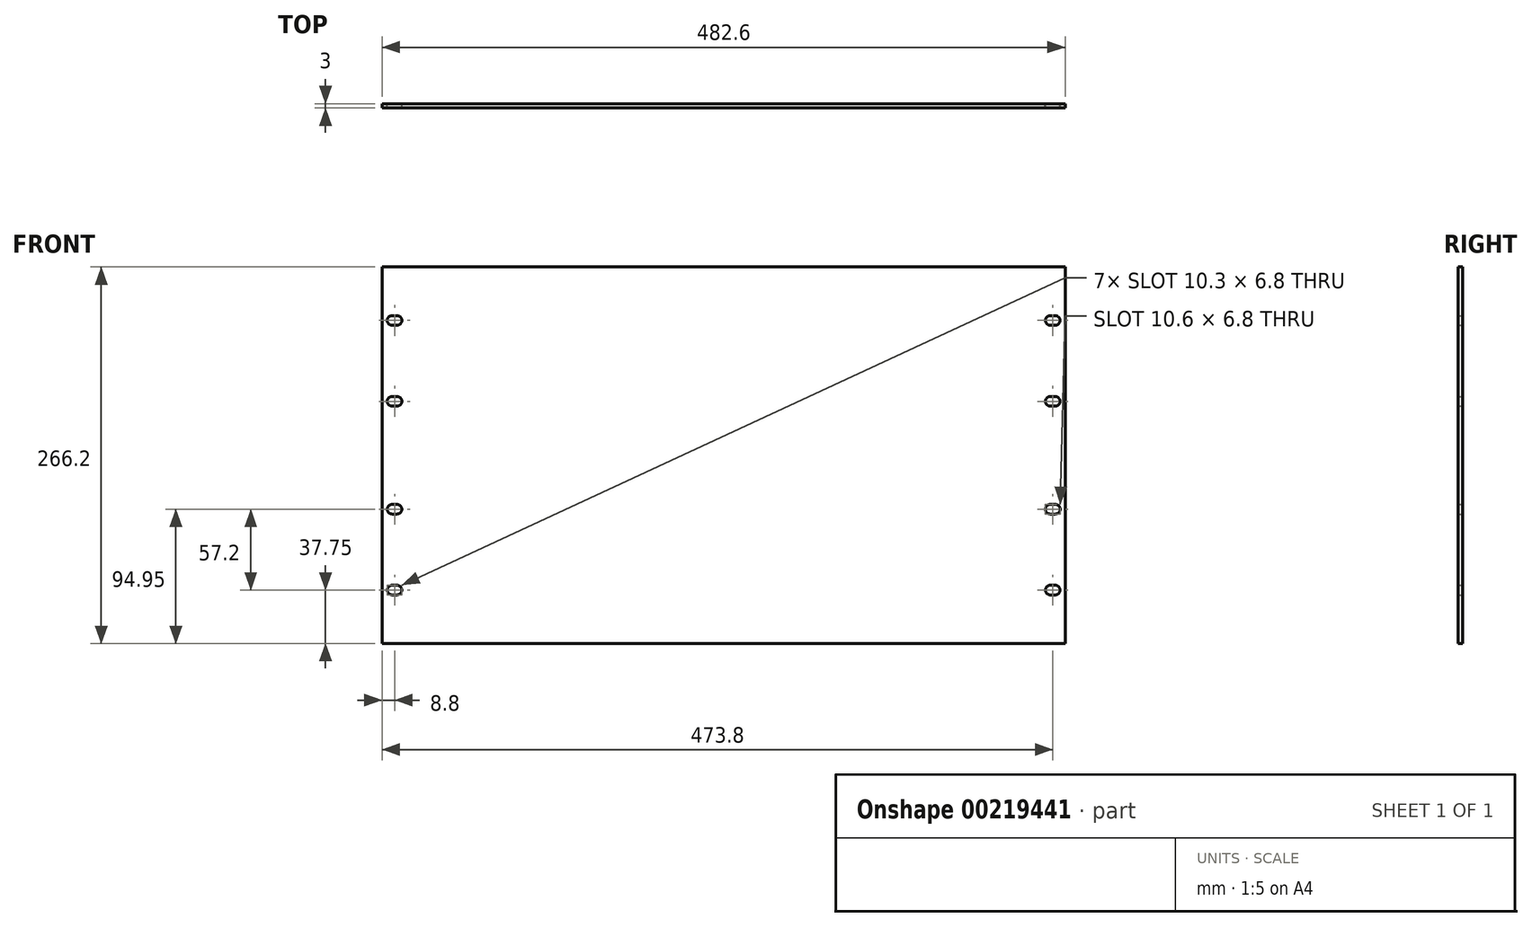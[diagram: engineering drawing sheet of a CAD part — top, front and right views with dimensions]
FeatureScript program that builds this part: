
annotation { "Feature Type Name" : "Feature", "Feature Type Description" : "" }
export const myFeature = defineFeature(function(context is Context, id is Id, definition is map)
    precondition{}
    {
        {
            var Q0;
            Q0=qCreatedBy(makeId("Front.planeOp"),FACE);
            var sketch = newSketch(context, id + "F0", { "sketchPlane" : qUnion([Q0])});
            skLineSegment(sketch, "E0.bottom", {"start": v(241.3, -133.1) * mm, "end": v(-241.3, -133.1) * mm});
            skLineSegment(sketch, "E0.top", {"start": v(241.3, 133.1) * mm, "end": v(-241.3, 133.1) * mm});
            skLineSegment(sketch, "E0.left", {"start": v(241.3, -133.1) * mm, "end": v(241.3, 133.1) * mm});
            skLineSegment(sketch, "E0.right", {"start": v(-241.3, -133.1) * mm, "end": v(-241.3, 133.1) * mm});
            skPoint(sketch, "E0.middle", {"position": v(0, 0) * mm});
            skSolve(sketch);
        }
        {
            var Q0;
            Q0=qSketchRegion(id+"F0",true);
            extrude(context, id + "F1", {"entities" : qUnion([Q0]), "oppositeDirection" : true, "depth" : 3 * mm});
        }
        {
            var Q0;
            Q0=makeQuery(id+"F1.opExtrude","CAP_FACE",FACE,{"disambiguationData":[OSD([sQuery(id+"F0.wireOp",EDGE,"E0.bottom"),sQuery(id+"F0.wireOp",EDGE,"E0.top"),sQuery(id+"F0.wireOp",EDGE,"E0.left"),sQuery(id+"F0.wireOp",EDGE,"E0.right")])],"isStart":false});
            var sketch = newSketch(context, id + "F2", { "sketchPlane" : qUnion([Q0])});
            skLineSegment(sketch, "E1.bottom", {"start": v(234.25, 91.95) * mm, "end": v(230.75, 91.95) * mm});
            skLineSegment(sketch, "E1.top", {"start": v(234.25, 98.75) * mm, "end": v(230.75, 98.75) * mm});
            skLineSegment(sketch, "E1.left", {"start": v(234.25, 91.95) * mm, "end": v(234.25, 98.75) * mm});
            skLineSegment(sketch, "E1.right", {"start": v(230.75, 91.95) * mm, "end": v(230.75, 98.75) * mm});
            skPoint(sketch, "E1.middle", {"position": v(232.5, 95.35) * mm});
            skArc(sketch, "E2", {"start": v(234.25, 91.95) * mm, "mid": v(237.65, 95.35) * mm, "end": v(234.25, 98.75) * mm});
            skArc(sketch, "E3", {"start": v(230.75, 98.75) * mm, "mid": v(227.35, 95.35) * mm, "end": v(230.75, 91.95) * mm});
            skSolve(sketch);
        }
        {
            var Q0;
            Q0=qSketchRegion(id+"F2",true);
            extrude(context, id + "F3", {"entities" : qUnion([Q0]), "operationType" : NewBodyOperationType.REMOVE, "oppositeDirection" : true, "depth" : 3 * mm});
        }
        {
            var Q0;
            Q0=makeQuery(id+"F1.opExtrude","CAP_FACE",FACE,{"disambiguationData":[OSD([sQuery(id+"F0.wireOp",EDGE,"E0.bottom"),sQuery(id+"F0.wireOp",EDGE,"E0.top"),sQuery(id+"F0.wireOp",EDGE,"E0.left"),sQuery(id+"F0.wireOp",EDGE,"E0.right")])],"isStart":false});
            var sketch = newSketch(context, id + "F4", { "sketchPlane" : qUnion([Q0])});
            skLineSegment(sketch, "E4.bottom", {"start": v(234.25, 34.75) * mm, "end": v(230.75, 34.75) * mm});
            skLineSegment(sketch, "E4.top", {"start": v(234.25, 41.55) * mm, "end": v(230.75, 41.55) * mm});
            skLineSegment(sketch, "E4.left", {"start": v(234.25, 34.75) * mm, "end": v(234.25, 41.55) * mm});
            skLineSegment(sketch, "E4.right", {"start": v(230.75, 34.75) * mm, "end": v(230.75, 41.55) * mm});
            skPoint(sketch, "E4.middle", {"position": v(232.5, 38.15) * mm});
            skArc(sketch, "E5", {"start": v(230.75, 41.55) * mm, "mid": v(227.35, 38.15) * mm, "end": v(230.75, 34.75) * mm});
            skArc(sketch, "E6", {"start": v(234.25, 34.75) * mm, "mid": v(237.65, 38.15) * mm, "end": v(234.25, 41.55) * mm});
            skSolve(sketch);
        }
        {
            var Q0;
            Q0=qSketchRegion(id+"F4",true);
            extrude(context, id + "F5", {"entities" : qUnion([Q0]), "operationType" : NewBodyOperationType.REMOVE, "oppositeDirection" : true, "depth" : 3 * mm});
        }
        {
            var Q0;
            Q0=makeQuery(id+"F1.opExtrude","CAP_FACE",FACE,{"disambiguationData":[OSD([sQuery(id+"F0.wireOp",EDGE,"E0.bottom"),sQuery(id+"F0.wireOp",EDGE,"E0.top"),sQuery(id+"F0.wireOp",EDGE,"E0.left"),sQuery(id+"F0.wireOp",EDGE,"E0.right")])],"isStart":false});
            var sketch = newSketch(context, id + "F6", { "sketchPlane" : qUnion([Q0])});
            skLineSegment(sketch, "E7.bottom", {"start": v(234.25, -41.55) * mm, "end": v(230.75, -41.55) * mm});
            skLineSegment(sketch, "E7.top", {"start": v(234.25, -34.75) * mm, "end": v(230.75, -34.75) * mm});
            skLineSegment(sketch, "E7.left", {"start": v(234.25, -41.55) * mm, "end": v(234.25, -34.75) * mm});
            skLineSegment(sketch, "E7.right", {"start": v(230.75, -41.55) * mm, "end": v(230.75, -34.75) * mm});
            skPoint(sketch, "E7.middle", {"position": v(232.5, -38.15) * mm});
            skArc(sketch, "E8", {"start": v(234.25, -41.55) * mm, "mid": v(237.65, -38.15) * mm, "end": v(234.25, -34.75) * mm});
            skArc(sketch, "E9", {"start": v(230.75, -34.75) * mm, "mid": v(227.35, -38.15) * mm, "end": v(230.75, -41.55) * mm});
            skSolve(sketch);
        }
        {
            var Q0;
            Q0=qSketchRegion(id+"F6",true);
            extrude(context, id + "F7", {"entities" : qUnion([Q0]), "operationType" : NewBodyOperationType.REMOVE, "oppositeDirection" : true, "depth" : 3 * mm});
        }
        {
            var Q0;
            Q0=makeQuery(id+"F1.opExtrude","CAP_FACE",FACE,{"disambiguationData":[OSD([sQuery(id+"F0.wireOp",EDGE,"E0.bottom"),sQuery(id+"F0.wireOp",EDGE,"E0.top"),sQuery(id+"F0.wireOp",EDGE,"E0.left"),sQuery(id+"F0.wireOp",EDGE,"E0.right")])],"isStart":false});
            var sketch = newSketch(context, id + "F8", { "sketchPlane" : qUnion([Q0])});
            skLineSegment(sketch, "E10.bottom", {"start": v(234.25, -91.95) * mm, "end": v(230.75, -91.95) * mm});
            skLineSegment(sketch, "E10.top", {"start": v(234.25, -98.75) * mm, "end": v(230.75, -98.75) * mm});
            skLineSegment(sketch, "E10.left", {"start": v(234.25, -91.95) * mm, "end": v(234.25, -98.75) * mm});
            skLineSegment(sketch, "E10.right", {"start": v(230.75, -91.95) * mm, "end": v(230.75, -98.75) * mm});
            skPoint(sketch, "E10.middle", {"position": v(232.5, -95.35) * mm});
            skArc(sketch, "E11", {"start": v(234.25, -98.75) * mm, "mid": v(237.65, -95.35) * mm, "end": v(234.25, -91.95) * mm});
            skArc(sketch, "E12", {"start": v(230.75, -91.95) * mm, "mid": v(227.35, -95.35) * mm, "end": v(230.75, -98.75) * mm});
            skSolve(sketch);
        }
        {
            var Q0;
            Q0=qSketchRegion(id+"F8",true);
            extrude(context, id + "F9", {"entities" : qUnion([Q0]), "operationType" : NewBodyOperationType.REMOVE, "oppositeDirection" : true, "depth" : 3 * mm});
        }
        {
            var Q0;
            Q0=makeQuery(id+"F1.opExtrude","CAP_FACE",FACE,{"disambiguationData":[OSD([sQuery(id+"F0.wireOp",EDGE,"E0.bottom"),sQuery(id+"F0.wireOp",EDGE,"E0.top"),sQuery(id+"F0.wireOp",EDGE,"E0.left"),sQuery(id+"F0.wireOp",EDGE,"E0.right")])],"isStart":false});
            var sketch = newSketch(context, id + "F10", { "sketchPlane" : qUnion([Q0])});
            skLineSegment(sketch, "E13.bottom", {"start": v(-230.75, 91.95) * mm, "end": v(-234.25, 91.95) * mm});
            skLineSegment(sketch, "E13.top", {"start": v(-230.75, 98.75) * mm, "end": v(-234.25, 98.75) * mm});
            skLineSegment(sketch, "E13.left", {"start": v(-230.75, 91.95) * mm, "end": v(-230.75, 98.75) * mm});
            skLineSegment(sketch, "E13.right", {"start": v(-234.25, 91.95) * mm, "end": v(-234.25, 98.75) * mm});
            skPoint(sketch, "E13.middle", {"position": v(-232.5, 95.35) * mm});
            skArc(sketch, "E14", {"start": v(-230.75, 91.95) * mm, "mid": v(-227.35, 95.35) * mm, "end": v(-230.75, 98.75) * mm});
            skArc(sketch, "E15", {"start": v(-234.25, 98.75) * mm, "mid": v(-237.65, 95.35) * mm, "end": v(-234.25, 91.95) * mm});
            skSolve(sketch);
        }
        {
            var Q0;
            Q0=makeQuery(id+"F10.imprint","IMPRINT",FACE,{"disambiguationData":[TD([[makeQuery(id+"F10.imprint","IMPRINT",EDGE,{"derivedFrom":sQuery(id+"F10.wireOp",EDGE,"E13.bottom")}),1.0]])]});
            var sketch = newSketch(context, id + "F11", { "sketchPlane" : qUnion([Q0])});
            skLineSegment(sketch, "E16.bottom", {"start": v(-234.25, 41.55) * mm, "end": v(-230.75, 41.55) * mm});
            skLineSegment(sketch, "E16.top", {"start": v(-234.25, 34.75) * mm, "end": v(-230.75, 34.75) * mm});
            skLineSegment(sketch, "E16.left", {"start": v(-234.25, 41.55) * mm, "end": v(-234.25, 34.75) * mm});
            skLineSegment(sketch, "E16.right", {"start": v(-230.75, 41.55) * mm, "end": v(-230.75, 34.75) * mm});
            skPoint(sketch, "E16.middle", {"position": v(-232.5, 38.15) * mm});
            skArc(sketch, "E17", {"start": v(-230.75, 34.75) * mm, "mid": v(-227.35, 38.15) * mm, "end": v(-230.75, 41.55) * mm});
            skArc(sketch, "E18", {"start": v(-234.25, 41.55) * mm, "mid": v(-237.65, 38.15) * mm, "end": v(-234.25, 34.75) * mm});
            skSolve(sketch);
        }
        {
            var Q0;
            Q0=makeQuery(id+"F10.imprint","IMPRINT",FACE,{"disambiguationData":[TD([[makeQuery(id+"F10.imprint","IMPRINT",EDGE,{"derivedFrom":sQuery(id+"F10.wireOp",EDGE,"E13.bottom")}),1.0]])]});
            var sketch = newSketch(context, id + "F12", { "sketchPlane" : qUnion([Q0])});
            skLineSegment(sketch, "E19.bottom", {"start": v(-230.6, -41.55) * mm, "end": v(-234.4, -41.55) * mm});
            skLineSegment(sketch, "E19.top", {"start": v(-230.6, -34.75) * mm, "end": v(-234.4, -34.75) * mm});
            skLineSegment(sketch, "E19.left", {"start": v(-230.6, -41.55) * mm, "end": v(-230.6, -34.75) * mm});
            skLineSegment(sketch, "E19.right", {"start": v(-234.4, -41.55) * mm, "end": v(-234.4, -34.75) * mm});
            skPoint(sketch, "E19.middle", {"position": v(-232.5, -38.15) * mm});
            skLineSegment(sketch, "E20.bottom", {"start": v(-230.75, -98.75) * mm, "end": v(-234.25, -98.75) * mm});
            skLineSegment(sketch, "E20.top", {"start": v(-230.75, -91.95) * mm, "end": v(-234.25, -91.95) * mm});
            skLineSegment(sketch, "E20.left", {"start": v(-230.75, -98.75) * mm, "end": v(-230.75, -91.95) * mm});
            skLineSegment(sketch, "E20.right", {"start": v(-234.25, -98.75) * mm, "end": v(-234.25, -91.95) * mm});
            skPoint(sketch, "E20.middle", {"position": v(-232.5, -95.35) * mm});
            skArc(sketch, "E21", {"start": v(-230.6, -41.55) * mm, "mid": v(-227.2, -38.15) * mm, "end": v(-230.6, -34.75) * mm});
            skArc(sketch, "E22", {"start": v(-234.4, -34.75) * mm, "mid": v(-237.8, -38.15) * mm, "end": v(-234.4, -41.55) * mm});
            skArc(sketch, "E23", {"start": v(-230.75, -98.75) * mm, "mid": v(-227.35, -95.35) * mm, "end": v(-230.75, -91.95) * mm});
            skArc(sketch, "E24", {"start": v(-234.25, -91.95) * mm, "mid": v(-237.65, -95.35) * mm, "end": v(-234.25, -98.75) * mm});
            skSolve(sketch);
        }
        {
            var Q0;
            Q0=qSketchRegion(id+"F12",true);
            var Q1;
            Q1=qSketchRegion(id+"F10",true);
            var Q2;
            Q2=qSketchRegion(id+"F11",true);
            extrude(context, id + "F13", {"entities" : qUnion([Q0, Q1, Q2]), "operationType" : NewBodyOperationType.REMOVE, "oppositeDirection" : true, "depth" : 3 * mm});
        }
    });
